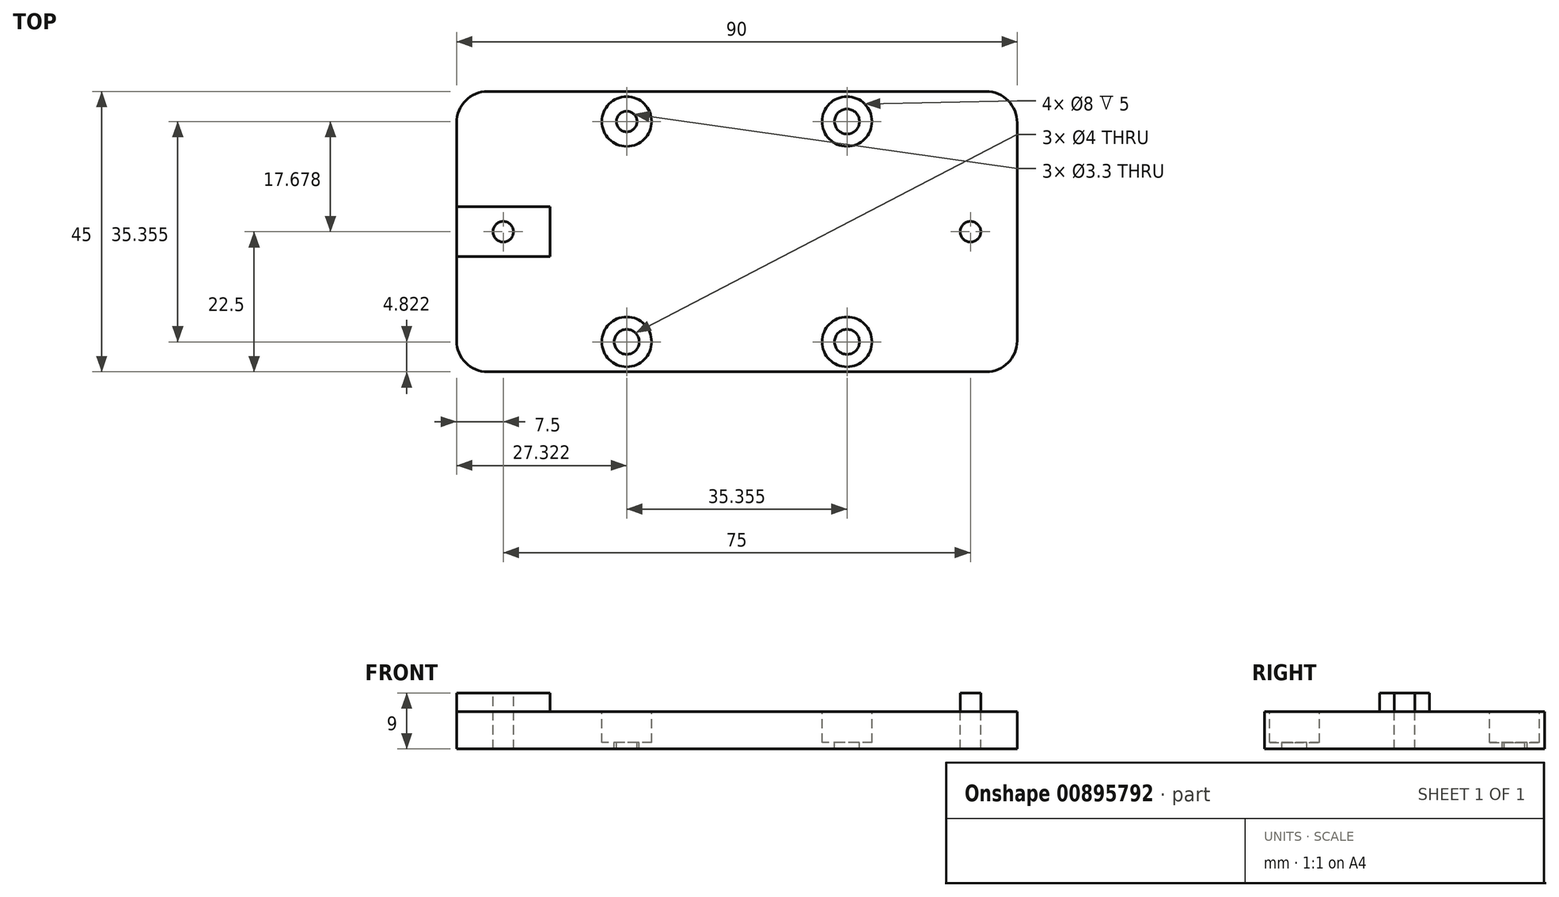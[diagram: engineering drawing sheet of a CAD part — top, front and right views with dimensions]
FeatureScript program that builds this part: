
annotation { "Feature Type Name" : "Feature", "Feature Type Description" : "" }
export const myFeature = defineFeature(function(context is Context, id is Id, definition is map)
    precondition{}
    {
        {
            var Q0;
            Q0=qCreatedBy(makeId("Top.planeOp"),FACE);
            var sketch = newSketch(context, id + "F0", { "sketchPlane" : qUnion([Q0])});
            skLineSegment(sketch, "E0.bottom", {"start": v(-40, 22.5) * mm, "end": v(40, 22.5) * mm});
            skLineSegment(sketch, "E0.top", {"start": v(-40, -22.5) * mm, "end": v(40, -22.5) * mm});
            skLineSegment(sketch, "E0.left", {"start": v(-45, 17.5) * mm, "end": v(-45, -17.5) * mm});
            skLineSegment(sketch, "E0.right", {"start": v(45, 17.5) * mm, "end": v(45, -17.5) * mm});
            skPoint(sketch, "E0.middle", {"position": v(0, 0) * mm});
            skCircle(sketch, "E1.1.0", {"center": v(-17.68, 17.68) * mm, "radius": 4 * mm});
            skCircle(sketch, "E1.1.1", {"center": v(-17.68, 17.68) * mm, "radius": 1.65 * mm});
            skCircle(sketch, "E1.3.0", {"center": v(-17.68, -17.68) * mm, "radius": 4 * mm});
            skCircle(sketch, "E1.3.1", {"center": v(-17.68, -17.68) * mm, "radius": 2 * mm});
            skPoint(sketch, "E2.visualSharp", {"position": v(-45, 22.5) * mm});
            skArc(sketch, "E2.filletArc", {"start": v(-40, 22.5) * mm, "mid": v(-43.54, 21.04) * mm, "end": v(-45, 17.5) * mm});
            skPoint(sketch, "E3.visualSharp", {"position": v(45, 22.5) * mm});
            skArc(sketch, "E3.filletArc", {"start": v(45, 17.5) * mm, "mid": v(43.54, 21.04) * mm, "end": v(40, 22.5) * mm});
            skPoint(sketch, "E4.visualSharp", {"position": v(45, -22.5) * mm});
            skArc(sketch, "E4.filletArc", {"start": v(40, -22.5) * mm, "mid": v(43.54, -21.04) * mm, "end": v(45, -17.5) * mm});
            skPoint(sketch, "E5.visualSharp", {"position": v(-45, -22.5) * mm});
            skArc(sketch, "E5.filletArc", {"start": v(-45, -17.5) * mm, "mid": v(-43.54, -21.04) * mm, "end": v(-40, -22.5) * mm});
            skCircle(sketch, "E6.1.5.0", {"center": v(17.68, -17.68) * mm, "radius": 4 * mm});
            skCircle(sketch, "E6.2.5.0", {"center": v(17.68, -17.68) * mm, "radius": 2 * mm});
            skCircle(sketch, "E6.1.7.0", {"center": v(17.68, 17.68) * mm, "radius": 4 * mm});
            skCircle(sketch, "E6.2.7.0", {"center": v(17.68, 17.68) * mm, "radius": 2 * mm});
            skCircle(sketch, "E7", {"center": v(-37.5, 0) * mm, "radius": 1.65 * mm});
            skCircle(sketch, "E8.MirrorC", {"center": v(37.5, 0) * mm, "radius": 1.65 * mm});
            skLineSegment(sketch, "E9", {"start": v(-45, 4) * mm, "end": v(-30, 4) * mm});
            skLineSegment(sketch, "E10", {"start": v(-30, 4) * mm, "end": v(-30, 0) * mm});
            skLineSegment(sketch, "E11.MirrorCS", {"start": v(-45, -4) * mm, "end": v(-30, -4) * mm});
            skLineSegment(sketch, "E12.MirrorCS", {"start": v(-30, -4) * mm, "end": v(-30, 0) * mm});
            skLineSegment(sketch, "E13.MirrorCS", {"start": v(45, 4) * mm, "end": v(30, 4) * mm});
            skLineSegment(sketch, "E14.MirrorCS", {"start": v(30, 4) * mm, "end": v(30, 0) * mm});
            skLineSegment(sketch, "E15.MirrorCS", {"start": v(30, -4) * mm, "end": v(30, 0) * mm});
            skLineSegment(sketch, "E16.MirrorCS", {"start": v(45, -4) * mm, "end": v(30, -4) * mm});
            skSolve(sketch);
        }
        {
            var Q0;
            Q0 = qSketchRegion(id + "F0", true);
            var Q1;
            Q1=makeQuery(id+"F0.imprint","IMPRINT",FACE,{"disambiguationData":[TD([[makeQuery(id+"F0.imprint","IMPRINT",EDGE,{"derivedFrom":sQuery(id+"F0.wireOp",EDGE,"E1.1.0")}),1.0]])]});
            var Q2;
            Q2=makeQuery(id+"F0.imprint","IMPRINT",FACE,{"disambiguationData":[TD([[makeQuery(id+"F0.imprint","IMPRINT",EDGE,{"derivedFrom":sQuery(id+"F0.wireOp",EDGE,"UzwqMxC6-Xfvl-kvK5-6X4W-a8Wug1Xq9vTY")}),-1.0]])]});
            var Q3;
            Q3=makeQuery(id+"F0.imprint","IMPRINT",FACE,{"disambiguationData":[TD([[makeQuery(id+"F0.imprint","IMPRINT",EDGE,{"derivedFrom":sQuery(id+"F0.wireOp",EDGE,"E1.3.0")}),1.0]])]});
            var Q4;
            Q4=makeQuery(id+"F0.imprint","IMPRINT",FACE,{"disambiguationData":[TD([[makeQuery(id+"F0.imprint","IMPRINT",EDGE,{"derivedFrom":sQuery(id+"F0.wireOp",EDGE,"E1.2.0")}),1.0]])]});
            var Q5;
            Q5=makeQuery(id+"F0.imprint","IMPRINT",FACE,{"disambiguationData":[TD([[makeQuery(id+"F0.imprint","IMPRINT",EDGE,{"derivedFrom":sQuery(id+"F0.wireOp",EDGE,"E6.1.7.0")}),1.0]])]});
            var Q6;
            Q6=makeQuery(id+"F0.imprint","IMPRINT",FACE,{"disambiguationData":[TD([[makeQuery(id+"F0.imprint","IMPRINT",EDGE,{"derivedFrom":sQuery(id+"F0.wireOp",EDGE,"E6.1.5.0")}),1.0]])]});
            var Q7;
            Q7=makeQuery(id+"F0.imprint","IMPRINT",FACE,{"disambiguationData":[TD([[makeQuery(id+"F0.imprint","IMPRINT",EDGE,{"derivedFrom":sQuery(id+"F0.wireOp",EDGE,"E6.1.4.0")}),1.0]])]});
            extrude(context, id + "F1", {"entities" : qUnion([Q0, Q1, Q2, Q3, Q4, Q5, Q6, Q7]), "oppositeDirection" : true, "depth" : 6 * mm, "offsetDistance" : 25 * mm});
        }
        {
            var Q0;
            Q0=makeQuery(id+"F0.imprint","IMPRINT",FACE,{"disambiguationData":[TD([[makeQuery(id+"F0.imprint","IMPRINT",EDGE,{"derivedFrom":sQuery(id+"F0.wireOp",EDGE,"E1.1.0")}),1.0]])]});
            var Q1;
            Q1=makeQuery(id+"F0.imprint","IMPRINT",FACE,{"disambiguationData":[TD([[makeQuery(id+"F0.imprint","IMPRINT",EDGE,{"derivedFrom":sQuery(id+"F0.wireOp",EDGE,"E1.1.1")}),1.0]])]});
            var Q2;
            Q2=makeQuery(id+"F0.imprint","IMPRINT",FACE,{"disambiguationData":[TD([[makeQuery(id+"F0.imprint","IMPRINT",EDGE,{"derivedFrom":sQuery(id+"F0.wireOp",EDGE,"UzwqMxC6-Xfvl-kvK5-6X4W-a8Wug1Xq9vTY")}),-1.0]])]});
            var Q3;
            Q3=makeQuery(id+"F0.imprint","IMPRINT",FACE,{"disambiguationData":[TD([[makeQuery(id+"F0.imprint","IMPRINT",EDGE,{"derivedFrom":sQuery(id+"F0.wireOp",EDGE,"E1.2.0")}),1.0]])]});
            var Q4;
            Q4=makeQuery(id+"F0.imprint","IMPRINT",FACE,{"disambiguationData":[TD([[makeQuery(id+"F0.imprint","IMPRINT",EDGE,{"derivedFrom":sQuery(id+"F0.wireOp",EDGE,"E1.3.0")}),1.0]])]});
            var Q5;
            Q5=makeQuery(id+"F0.imprint","IMPRINT",FACE,{"disambiguationData":[TD([[makeQuery(id+"F0.imprint","IMPRINT",EDGE,{"derivedFrom":sQuery(id+"F0.wireOp",EDGE,"E6.1.4.0")}),1.0]])]});
            var Q6;
            Q6=makeQuery(id+"F0.imprint","IMPRINT",FACE,{"disambiguationData":[TD([[makeQuery(id+"F0.imprint","IMPRINT",EDGE,{"derivedFrom":sQuery(id+"F0.wireOp",EDGE,"E6.1.5.0")}),1.0]])]});
            var Q7;
            Q7=makeQuery(id+"F0.imprint","IMPRINT",FACE,{"disambiguationData":[TD([[makeQuery(id+"F0.imprint","IMPRINT",EDGE,{"derivedFrom":sQuery(id+"F0.wireOp",EDGE,"E6.1.7.0")}),1.0]])]});
            extrude(context, id + "F2", {"entities" : qUnion([Q0, Q1, Q2, Q3, Q4, Q5, Q6, Q7]), "operationType" : NewBodyOperationType.REMOVE, "oppositeDirection" : true, "depth" : 5 * mm, "offsetDistance" : 25 * mm});
        }
        {
            var Q0;
            Q0=makeQuery(id+"F0.imprint","IMPRINT",FACE,{"disambiguationData":[TD([[makeQuery(id+"F0.imprint","IMPRINT",EDGE,{"derivedFrom":sQuery(id+"F0.wireOp",EDGE,"E7")}),-1.0]])]});
            var Q1;
            Q1=makeQuery(id+"F0.imprint","IMPRINT",FACE,{"disambiguationData":[TD([[makeQuery(id+"F0.imprint","IMPRINT",EDGE,{"derivedFrom":sQuery(id+"F0.wireOp",EDGE,"E8.MirrorC")}),1.0]])]});
            extrude(context, id + "F3", {"entities" : qUnion([Q0, Q1]), "operationType" : NewBodyOperationType.ADD, "depth" : 3 * mm, "offsetDistance" : 25 * mm});
        }
    });
